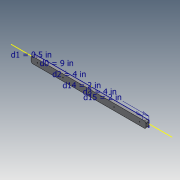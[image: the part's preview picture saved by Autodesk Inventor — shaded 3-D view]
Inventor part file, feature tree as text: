
AUTODESK INVENTOR PART (.ipt)
format: ipt  version: 2018.3 (Build 223284000, 284)  size: 111,616 bytes
history: native  units: in
note: dims shown in document units (in); Inventor stores cm internally (conversion verified against a paired STEP export)
features: sketch x1, extrude x1, hole x1, fillet x1
ambient origin geometry x8: Origin, YZ Plane, XZ Plane, XY Plane, X Axis, Y Axis, Z Axis, Center Point
bodies: Solid1 (feature_tree)
feature tree (4):
  sketch  "Sketch1"  dims[d0=9.0in d1=0.5in d2=4.0in d3=4.0in d4=0.23in d5=0.0in d6=0.06in d7=0.75in d8=0.375in d9=0.25in d10=0.5635in d11=1.0in d12=0.8108in d13=0.125in d14=2.0in d15=2.0in]
  extrude  "Extrusion1"  Depth=0.5in
  hole  "Hole1"  [1 undecoded]
  fillet  "Fillet1"  Radius=4.0in
note: 1 required parameter value undecoded (feature->parameter linkage not recoverable at this tier; creation-order binding heuristic only, values carry confidence <= 0.55)
